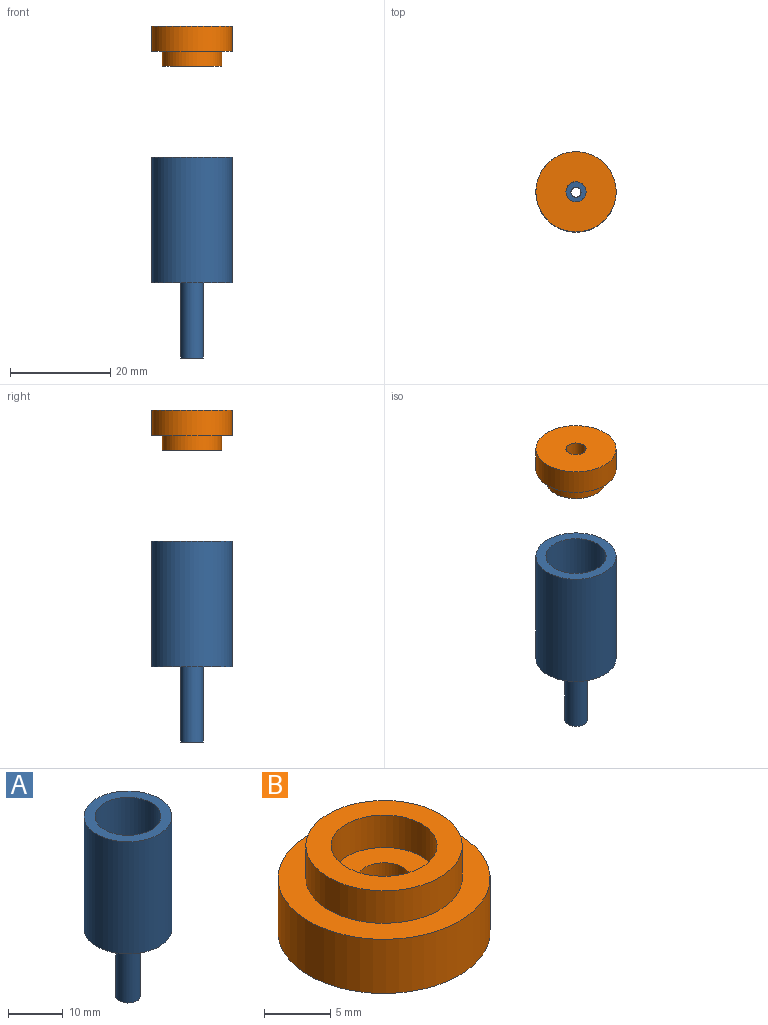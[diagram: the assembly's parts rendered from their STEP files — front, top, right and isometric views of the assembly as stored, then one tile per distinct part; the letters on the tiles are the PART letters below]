
ASSEMBLY  parts=2 mates=1
PART A: 8 faces, bbox 16x16x40 mm
  f0: plane 12x12mm, normal (0,0,1), area 110mm2, adj f1,f4
  f1: cylinder r=1mm len=18mm, axis (0,0,-1), area 113.1mm2, adj f0,f7
  f2: cylinder r=8mm len=25mm, axis (0,0,-1), area 1256.6mm2, adj f3,f5
  f3: plane 16x16mm, normal (0,0,-1), area 185.2mm2, adj f2,f6
  f4: cylinder r=6mm len=22mm, axis (0,0,-1), area 829.4mm2, adj f0,f5
  f5: plane 16x16mm, normal (0,0,1), area 88mm2, adj f2,f4
  f6: cylinder r=2.25mm len=15mm, axis (0,0,1), area 212.1mm2, adj f3,f7
  f7: plane 4.5x4.5mm, normal (0,0,-1), area 12.8mm2, adj f1,f6
PART B: 8 faces, bbox 16x16x8 mm
  f0: plane 8x8mm, normal (0,0,1), area 37.7mm2, adj f1,f5
  f1: cylinder r=2mm len=5mm, axis (0,0,-1), area 62.8mm2, adj f0,f4
  f2: cylinder r=8mm len=16mm, axis (0,0,-1), area 251.3mm2, adj f3,f4
  f3: plane 16x16mm, normal (0,0,1), area 91.7mm2, adj f2,f6
  f4: plane 16x16mm, normal (0,0,-1), area 188.5mm2, adj f1,f2
  f5: cylinder r=4mm len=8mm, axis (0,0,-1), area 75.4mm2, adj f0,f7
  f6: cylinder r=5.9mm len=11.8mm, axis (0,0,-1), area 111.2mm2, adj f3,f7
  f7: plane 11.8x11.8mm, normal (0,0,1), area 59.1mm2, adj f5,f6
PLACE A t=(4.57,-1.26,25.09)mm
PLACE B rot(axis=(0,1,0),180deg) t=(4.57,-1.26,76.3)mm
MATE slider A.f2 <-> B.f2  axis (0,0,-1) through (4.57,-1.26,50.09)mm
